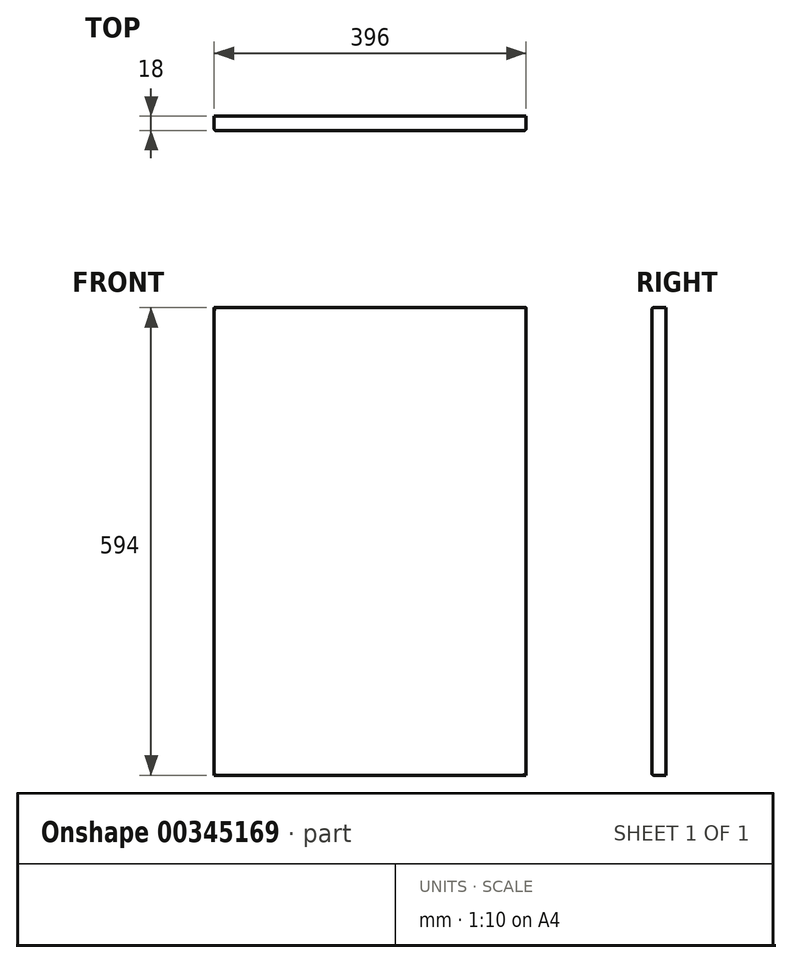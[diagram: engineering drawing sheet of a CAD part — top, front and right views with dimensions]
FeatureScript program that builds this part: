
annotation { "Feature Type Name" : "Feature", "Feature Type Description" : "" }
export const myFeature = defineFeature(function(context is Context, id is Id, definition is map)
    precondition{}
    {
        {
            var Q0;
            Q0=qCreatedBy(makeId("Front.planeOp"),FACE);
            var sketch = newSketch(context, id + "F0", { "sketchPlane" : qUnion([Q0])});
            skLineSegment(sketch, "E0.bottom", {"start": v(0, 0) * mm, "end": v(47.55, 0) * mm});
            skLineSegment(sketch, "E0.top", {"start": v(0, 38.08) * mm, "end": v(47.55, 38.08) * mm});
            skLineSegment(sketch, "E0.left", {"start": v(0, 0) * mm, "end": v(0, 38.08) * mm});
            skLineSegment(sketch, "E0.right", {"start": v(47.55, 0) * mm, "end": v(47.55, 38.08) * mm});
            skSolve(sketch);
        }
        {
            var Q0;
            Q0=makeQuery(id+"F0.imprint","IMPRINT",FACE,{"disambiguationData":[TD([[makeQuery(id+"F0.imprint","IMPRINT",EDGE,{"derivedFrom":sQuery(id+"F0.wireOp",EDGE,"E0.bottom")}),1.0]])]});
            extrude(context, id + "F1", {"entities" : qUnion([Q0]), "depth" : 18 * mm});
        }
        {
            var Q0;
            Q0=makeQuery(id+"F1.opExtrude","SWEPT_FACE",FACE,{"disambiguationData":[OSD([sQuery(id+"F0.wireOp",EDGE,"E0.left")])]});
            extrude(context, id + "F2", {"entities" : qUnion([Q0]), "operationType" : NewBodyOperationType.ADD, "oppositeDirection" : true, "depth" : 396 * mm});
        }
        {
            var Q0;
            {var subQ0=sQuery(id+"F0.wireOp",EDGE,"E0.bottom");Q0=makeQuery(id+"F2.boolean.opBoolean","MERGE",FACE,{"derivedFrom":[makeQuery(id+"F1.opExtrude","SWEPT_FACE",FACE,{"disambiguationData":[OSD([subQ0])]}),makeQuery(id+"F2.opExtrude","SWEPT_FACE",FACE,{"disambiguationData":[OSD([subQ0,sQuery(id+"F0.wireOp",EDGE,"E0.left")])]})]});}
            extrude(context, id + "F3", {"entities" : qUnion([Q0]), "operationType" : NewBodyOperationType.ADD, "oppositeDirection" : true, "depth" : 594 * mm});
        }
        {
            var Q0;
            {var subQ0=sQuery(id+"F0.wireOp",EDGE,"E0.left");var subQ1=sQuery(id+"F0.wireOp",EDGE,"E0.bottom");Q0=makeQuery(id+"F3.boolean.opBoolean","MERGE",FACE,{"derivedFrom":[makeQuery(id+"F2.boolean.opBoolean","MERGE",FACE,{"derivedFrom":[makeQuery(id+"F1.opExtrude","CAP_FACE",FACE,{"disambiguationData":[OSD([subQ1,sQuery(id+"F0.wireOp",EDGE,"E0.top"),subQ0,sQuery(id+"F0.wireOp",EDGE,"E0.right")])],"isStart":false}),makeQuery(id+"F2.opExtrude","SWEPT_FACE",FACE,{"disambiguationData":[OSD([subQ0]),TDD([makeQuery(id+"F1.opExtrude","CAP_EDGE",EDGE,{"disambiguationData":[OSD([subQ0])],"isStart":false})])]})]}),makeQuery(id+"F3.opExtrude","SWEPT_FACE",FACE,{"disambiguationData":[OSD([subQ1,subQ0]),TDD([makeQuery(id+"F2.boolean.opBoolean","MERGE",EDGE,{"derivedFrom":[makeQuery(id+"F1.opExtrude","CAP_EDGE",EDGE,{"disambiguationData":[OSD([subQ1])],"isStart":false}),makeQuery(id+"F2.opExtrude","SWEPT_EDGE",EDGE,{"disambiguationData":[OSD([subQ1,subQ0]),TDD([makeQuery(id+"F1.opExtrude","CAP_VERTEX",VERTEX,{"disambiguationData":[OSD([subQ1,subQ0])],"isStart":false})])]})]})])]})]});}
            fillet(context, id + "F4", {"entities" : qUnion([Q0]), "radius" : 2 * mm, "tangentPropagation" : true, "allowEdgeOverflow" : false});
        }
    });
